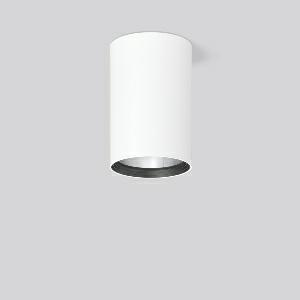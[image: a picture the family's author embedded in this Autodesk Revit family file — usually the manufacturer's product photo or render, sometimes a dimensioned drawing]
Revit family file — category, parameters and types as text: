
# Revit family: heledon_maxi_a_931217_002_e34e
name_source: partatom
category: Lighting Fixtures
units: mm (PartAtom-declared; Revit-internal decimal feet)

## family parameters
Cut with Voids When Loaded = No
Host = Face
Light Source = No
Part Type = Normal
Room Calculation Point = No
Round Connector Dimension = Use Diameter
Shared = No

## types (1)
- HELEDON maxi A (1 x LED Modul 930, 3350 lm, 3000)
    Apparent Load = 25 VA
    Approval mark = CE
    CIE Flux Codes = 100 100 100 100 100
    Color Rendering = 90
    Color Temperature = 3000
    Default Elevation = 1800 mm
    Description = Series: HELEDON maxi
Cylindrical surface-mounted downlight. Housing: die-cast aluminium, powder-coated. Internal ceiling frame polycarbonate with bayonet mounting. Black plastic ring and recessed LED to prevent glare from the side. Optical assembly with reflector made of MIRO-Silver with 98% total light reflection for outstanding efficiency - can be changed without tools. Best colour rendering index Ra>90. Suitable for Ceiling mounting. Easy installation with a separate ceiling frame with bayonet mounting and plug connection. Driver integrated. Connected via plug-in connector. High quality converter without flickering and stroboscopic effect. The following accessories can be mounted without use of tools: interchangeable lenses, decorative glasses, honeycomb louvre, clear and frosted diffusers, white interchangeable plastic ring. 
Colour: traffic white, matt (RAL 9016)
Diameter: 123 mm
Height: 183 mm
Lamp: LED
Socket: without socket
Colour temperature: 3000K
Colour rendering index (CRI): 92
System power: 25 W
Rated luminous flux: 3350 lm
Luminous efficiency: 134 lm/W
Control gear: Regulated power supply
Protection class: I
Type of protection: IP 20
    Height = 183 mm
    Lamp = 1 x LED Modul 930
    Lamp Light Flux = 3350 lm
    Lamp count = 1
    Length = 123 mm
    Lifetime = 50000 h
    Luminous efficacy = 134 lm/W
    Manufacturer = RZB
    ModVariant = No
    Model = 931217.002
    Mounting Place = Ceiling
    Mounting Type = Surface mounted
    Number of Poles = 1
    OnlyDefault = Yes
    Power Factor = 1
    Product Name = HELEDON maxi A
    Product group = Surface mounted downlights
    ProductGroupID = 302
    Protection Class = Protection class I
    Protection Degree = IP 20
    RLX_Detail_Level = 1
    RLX_Emergency_Light_Flux = 0 lm
    RLX_Emergency_Type = 0
    RLX_Emergency_Type_DB = No
    RlxData = <blob elided: 96181 chars, md5=51f03264>
    Socket = socket
    Standby Power = 0 W
    System Light Flux = 3350 lm
    System Power = 25 W
    Type Comments = Product without accessories
    Type Image = 931192.002.jpg
    URL = http://relux.com
    VarID = ---
    Voltage = 230 V
    Voltage Range = 220-240 V
    Weight = 0.00 kg
    Width = 0 mm  [stored 0 ft]

note: [stored X ft] marks values corroborated as IEEE doubles in the binary element streams (Revit-internal decimal feet)

## geometry (parser evidence)
native form markers: Blend x4, Sweep x11
no freeform markers — native parametric forms only
